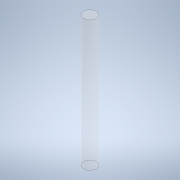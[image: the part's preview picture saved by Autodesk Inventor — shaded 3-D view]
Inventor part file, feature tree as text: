
AUTODESK INVENTOR PART (.ipt)
format: ipt  version: 2022.4 (Build 264492010, 492A)  size: 95,744 bytes
history: native  units: mm
features: extrude x1, sketch x1
ambient origin geometry x8: Origin, YZ Plane, XZ Plane, XY Plane, X Axis, Y Axis, Z Axis, Center Point
bodies: Solid1 (feature_tree)
feature tree (2):
  extrude  "Extrusion1"  Depth=50.0mm TaperAngle=0.0deg
  sketch  "Sketch1"  dims[d0=4.8mm d1=50.0mm d2=0.0mm]
